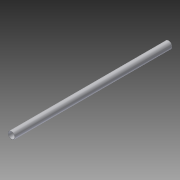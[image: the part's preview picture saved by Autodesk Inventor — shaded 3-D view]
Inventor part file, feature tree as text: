
AUTODESK INVENTOR PART (.ipt)
format: ipt  version: 2014 (Build 180170000, 170)  size: 71,680 bytes
history: native  units: in
note: dims shown in document units (in); Inventor stores cm internally (conversion verified against a paired STEP export)
features: extrude x1, sketch x1
ambient origin geometry x8: Origin, YZ Plane, XZ Plane, XY Plane, X Axis, Y Axis, Z Axis, Center Point
bodies: Solid1 (feature_tree)
feature tree (2):
  extrude  "Extrusion1"  Depth=52.0in
  sketch  "Sketch1"  dims[d0=2.375in d1=0.154in d2=52.0in d3=0.0in]
